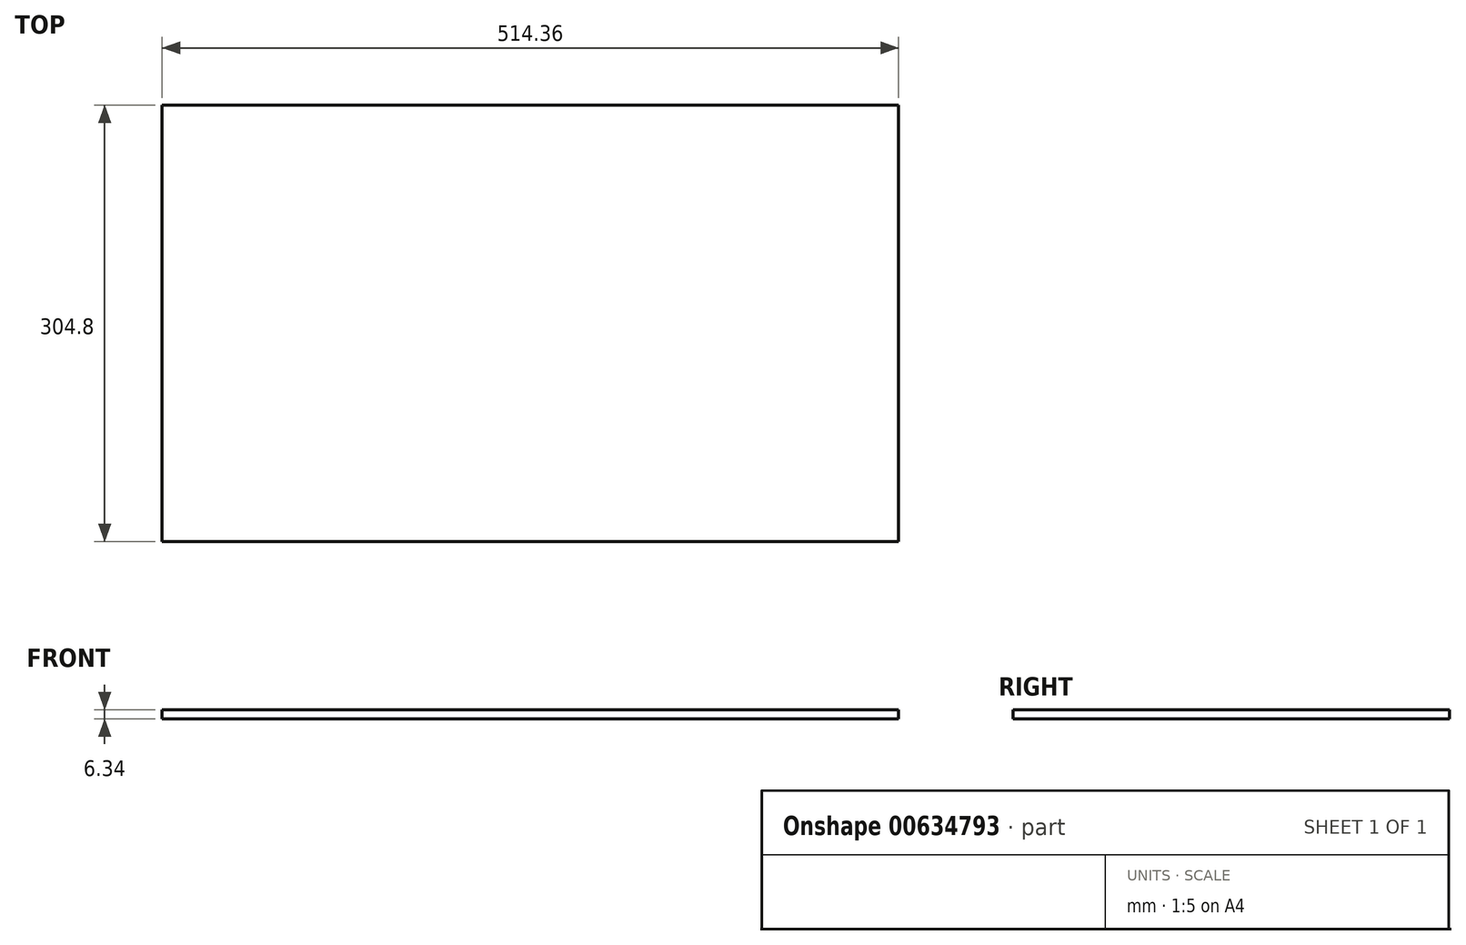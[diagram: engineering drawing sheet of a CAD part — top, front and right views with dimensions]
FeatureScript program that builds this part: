
annotation { "Feature Type Name" : "Feature", "Feature Type Description" : "" }
export const myFeature = defineFeature(function(context is Context, id is Id, definition is map)
    precondition{}
    {
        {
            var Q0;
            Q0=qCreatedBy(makeId("Front.planeOp"),FACE);
            var sketch = newSketch(context, id + "F0", { "sketchPlane" : qUnion([Q0])});
            skLineSegment(sketch, "E0.bottom", {"start": v(-257.18, 3.18) * mm, "end": v(257.18, 3.18) * mm});
            skLineSegment(sketch, "E0.top", {"start": v(-257.18, -3.18) * mm, "end": v(257.18, -3.18) * mm});
            skLineSegment(sketch, "E0.left", {"start": v(-257.18, 3.18) * mm, "end": v(-257.18, -3.18) * mm});
            skLineSegment(sketch, "E0.right", {"start": v(257.18, 3.18) * mm, "end": v(257.18, -3.18) * mm});
            skLineSegment(sketch, "E1", {"start": v(-257.18, 3.18) * mm, "end": v(257.18, -3.18) * mm, "construction": true});
            skSolve(sketch);
        }
        {
            var Q0;
            Q0=qSketchRegion(id+"F0",true);
            extrude(context, id + "F1", {"entities" : qUnion([Q0]), "endBound" : BoundingType.SYMMETRIC, "depth" : 304.8 * mm, "offsetDistance" : 25.4 * mm});
        }
    });
